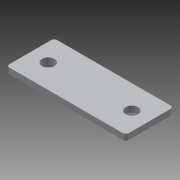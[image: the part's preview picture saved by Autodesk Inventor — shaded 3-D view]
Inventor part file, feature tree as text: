
AUTODESK INVENTOR PART (.ipt)
format: ipt  version: 2013 (Build 170138000, 138)  size: 85,504 bytes
history: native  units: in
note: dims shown in document units (in); Inventor stores cm internally (conversion verified against a paired STEP export)
features: extrude x1, fillet x1, sketch x1
ambient origin geometry x8: Origin, YZ Plane, XZ Plane, XY Plane, X Axis, Y Axis, Z Axis, Center Point
bodies: Solid1 (feature_tree)
feature tree (3):
  extrude  "Extrusion1"  Depth=1.0in
  fillet  "Fillet1"  Radius=1.75in
  sketch  "Sketch1"  dims[d0=2.5in d2=1.0in d3=1.75in d4=0.26in d5=0.125in d6=0.0in d7=0.0625in]
